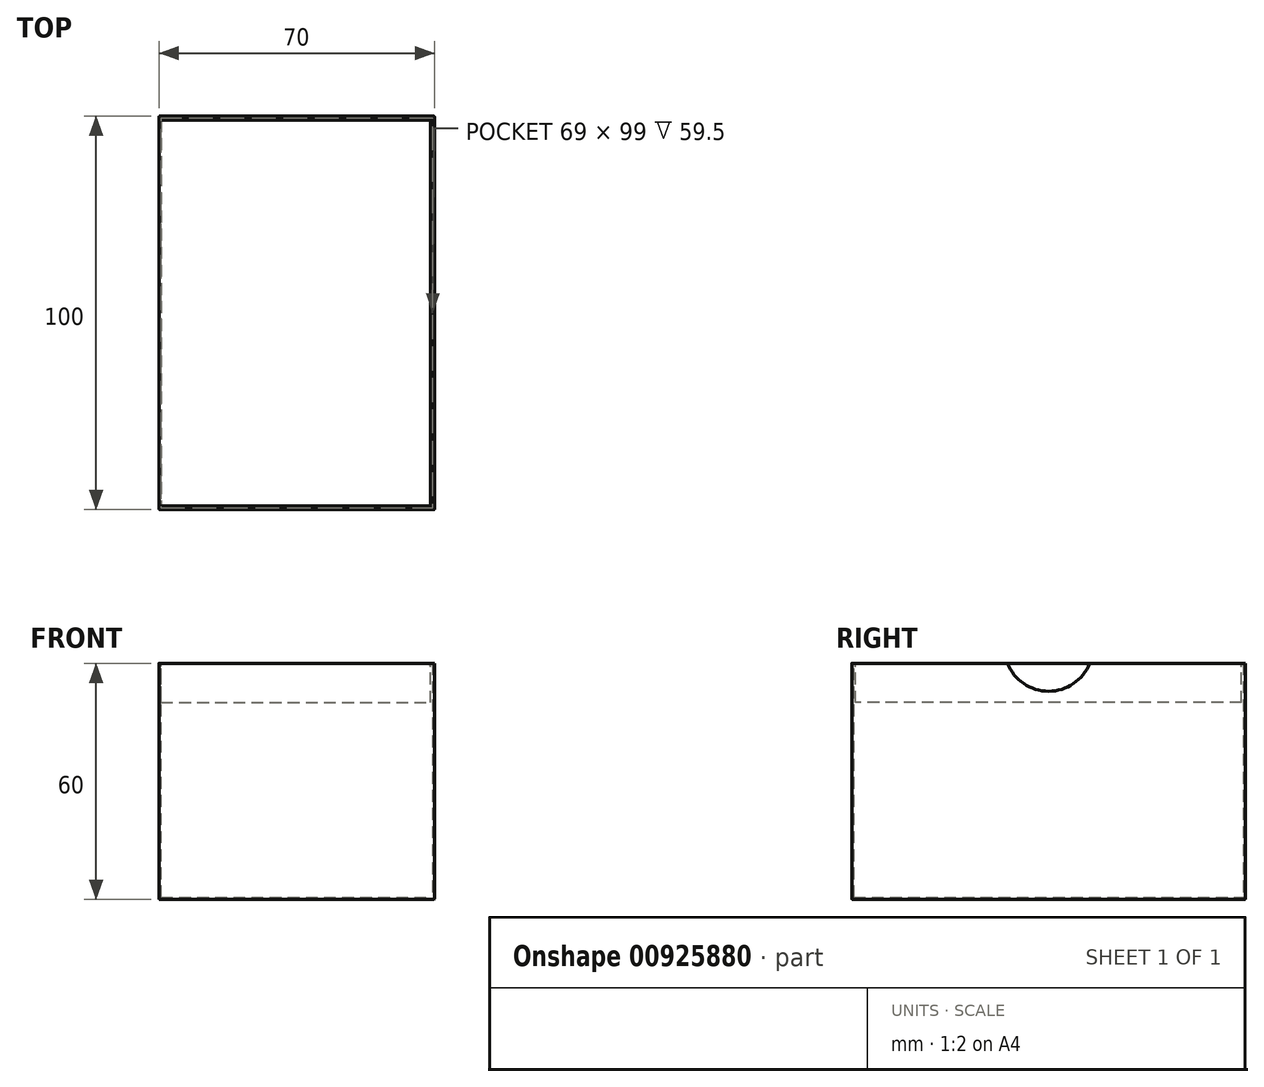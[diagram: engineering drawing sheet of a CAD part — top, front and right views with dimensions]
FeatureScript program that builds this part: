
annotation { "Feature Type Name" : "Feature", "Feature Type Description" : "" }
export const myFeature = defineFeature(function(context is Context, id is Id, definition is map)
    precondition{}
    {
        {
            var Q0;
            Q0=qCreatedBy(makeId("Top.planeOp"),FACE);
            var sketch = newSketch(context, id + "F0", { "sketchPlane" : qUnion([Q0])});
            skLineSegment(sketch, "E0.bottom", {"start": v(35, 50) * mm, "end": v(-35, 50) * mm});
            skLineSegment(sketch, "E0.top", {"start": v(35, -50) * mm, "end": v(-35, -50) * mm});
            skLineSegment(sketch, "E0.left", {"start": v(35, 50) * mm, "end": v(35, -50) * mm});
            skLineSegment(sketch, "E0.right", {"start": v(-35, 50) * mm, "end": v(-35, -50) * mm});
            skPoint(sketch, "E0.middle", {"position": v(0, 0) * mm});
            skSolve(sketch);
        }
        {
            var Q0;
            Q0 = qSketchRegion(id + "F0", true);
            extrude(context, id + "F1", {"entities" : qUnion([Q0]), "depth" : 60 * mm, "offsetDistance" : 25 * mm});
        }
        {
            var Q0;
            Q0=makeQuery(id+"F1.opExtrude","SWEPT_EDGE",EDGE,{"disambiguationData":[OSD([sQuery(id+"F0.wireOp",EDGE,"E0.top"),sQuery(id+"F0.wireOp",EDGE,"E0.left")])]});
            var Q1;
            Q1=makeQuery(id+"F1.opExtrude","CAP_FACE",FACE,{"disambiguationData":[OSD([sQuery(id+"F0.wireOp",EDGE,"E0.bottom"),sQuery(id+"F0.wireOp",EDGE,"E0.top"),sQuery(id+"F0.wireOp",EDGE,"E0.left"),sQuery(id+"F0.wireOp",EDGE,"E0.right")])],"isStart":true});
            var Q2;
            Q2=makeQuery(id+"F1.opExtrude","SWEPT_EDGE",EDGE,{"disambiguationData":[OSD([sQuery(id+"F0.wireOp",EDGE,"E0.bottom"),sQuery(id+"F0.wireOp",EDGE,"E0.left")])]});
            var Q3;
            Q3=makeQuery(id+"F1.opExtrude","SWEPT_EDGE",EDGE,{"disambiguationData":[OSD([sQuery(id+"F0.wireOp",EDGE,"E0.bottom"),sQuery(id+"F0.wireOp",EDGE,"E0.right")])]});
            var Q4;
            Q4=makeQuery(id+"F1.opExtrude","SWEPT_EDGE",EDGE,{"disambiguationData":[OSD([sQuery(id+"F0.wireOp",EDGE,"E0.top"),sQuery(id+"F0.wireOp",EDGE,"E0.right")])]});
            fillet(context, id + "F2", {"entities" : qUnion([Q0, Q1, Q2, Q3, Q4]), "radius" : 0.2 * mm, "tangentPropagation" : true, "allowEdgeOverflow" : false});
        }
        {
            var Q0;
            Q0=makeQuery(id+"F1.opExtrude","CAP_FACE",FACE,{"disambiguationData":[OSD([sQuery(id+"F0.wireOp",EDGE,"E0.bottom"),sQuery(id+"F0.wireOp",EDGE,"E0.top"),sQuery(id+"F0.wireOp",EDGE,"E0.left"),sQuery(id+"F0.wireOp",EDGE,"E0.right")])],"isStart":false});
            shell(context, id + "F3", {"entities" : qUnion([Q0]), "thickness" : 0.5 * mm});
        }
        {
            var Q0;
            Q0=makeQuery(id+"F1.opExtrude","CAP_FACE",FACE,{"disambiguationData":[OSD([sQuery(id+"F0.wireOp",EDGE,"E0.bottom"),sQuery(id+"F0.wireOp",EDGE,"E0.top"),sQuery(id+"F0.wireOp",EDGE,"E0.left"),sQuery(id+"F0.wireOp",EDGE,"E0.right")])],"isStart":false});
            var sketch = newSketch(context, id + "F4", { "sketchPlane" : qUnion([Q0])});
            skLineSegment(sketch, "E1.bottom", {"start": v(-34.5, -49) * mm, "end": v(34, -49) * mm});
            skLineSegment(sketch, "E1.top", {"start": v(-34.5, 49) * mm, "end": v(34, 49) * mm});
            skLineSegment(sketch, "E1.left", {"start": v(-34.5, -49) * mm, "end": v(-34.5, 49) * mm});
            skLineSegment(sketch, "E1.right", {"start": v(34, -49) * mm, "end": v(34, 49) * mm});
            skSolve(sketch);
        }
        {
            var Q0;
            Q0 = qSketchRegion(id + "F4", true);
            extrude(context, id + "F5", {"entities" : qUnion([Q0]), "operationType" : NewBodyOperationType.ADD, "oppositeDirection" : true, "depth" : 0.5 * mm, "offsetDistance" : 25 * mm});
        }
        {
            var Q0;
            Q0 = qSketchRegion(id + "F4", true);
            extrude(context, id + "F6", {"entities" : qUnion([Q0]), "operationType" : NewBodyOperationType.ADD, "oppositeDirection" : true, "depth" : 10 * mm, "offsetDistance" : 25 * mm});
        }
        {
            var Q0;
            Q0=makeQuery(id+"F5.opExtrude","CAP_EDGE",EDGE,{"disambiguationData":[OSD([sQuery(id+"F4.wireOp",EDGE,"E1.right")])],"isStart":true});
            fillet(context, id + "F7", {"entities" : qUnion([Q0]), "radius" : 1 * mm, "tangentPropagation" : true, "allowEdgeOverflow" : false});
        }
        {
            var Q0;
            Q0=makeQuery(id+"F1.opExtrude","SWEPT_FACE",FACE,{"disambiguationData":[OSD([sQuery(id+"F0.wireOp",EDGE,"E0.left")])]});
            var sketch = newSketch(context, id + "F8", { "sketchPlane" : qUnion([Q0])});
            skArc(sketch, "E2", {"start": v(-10.43, 60) * mm, "mid": v(0, 52.88) * mm, "end": v(10.43, 60) * mm});
            skLineSegment(sketch, "E3", {"start": v(-10.43, 60) * mm, "end": v(10.43, 60) * mm});
            skSolve(sketch);
        }
        {
            var Q0;
            Q0 = qSketchRegion(id + "F8", true);
            extrude(context, id + "F9", {"entities" : qUnion([Q0]), "operationType" : NewBodyOperationType.REMOVE, "oppositeDirection" : true, "depth" : 0.5 * mm, "offsetDistance" : 25 * mm});
        }
    });
